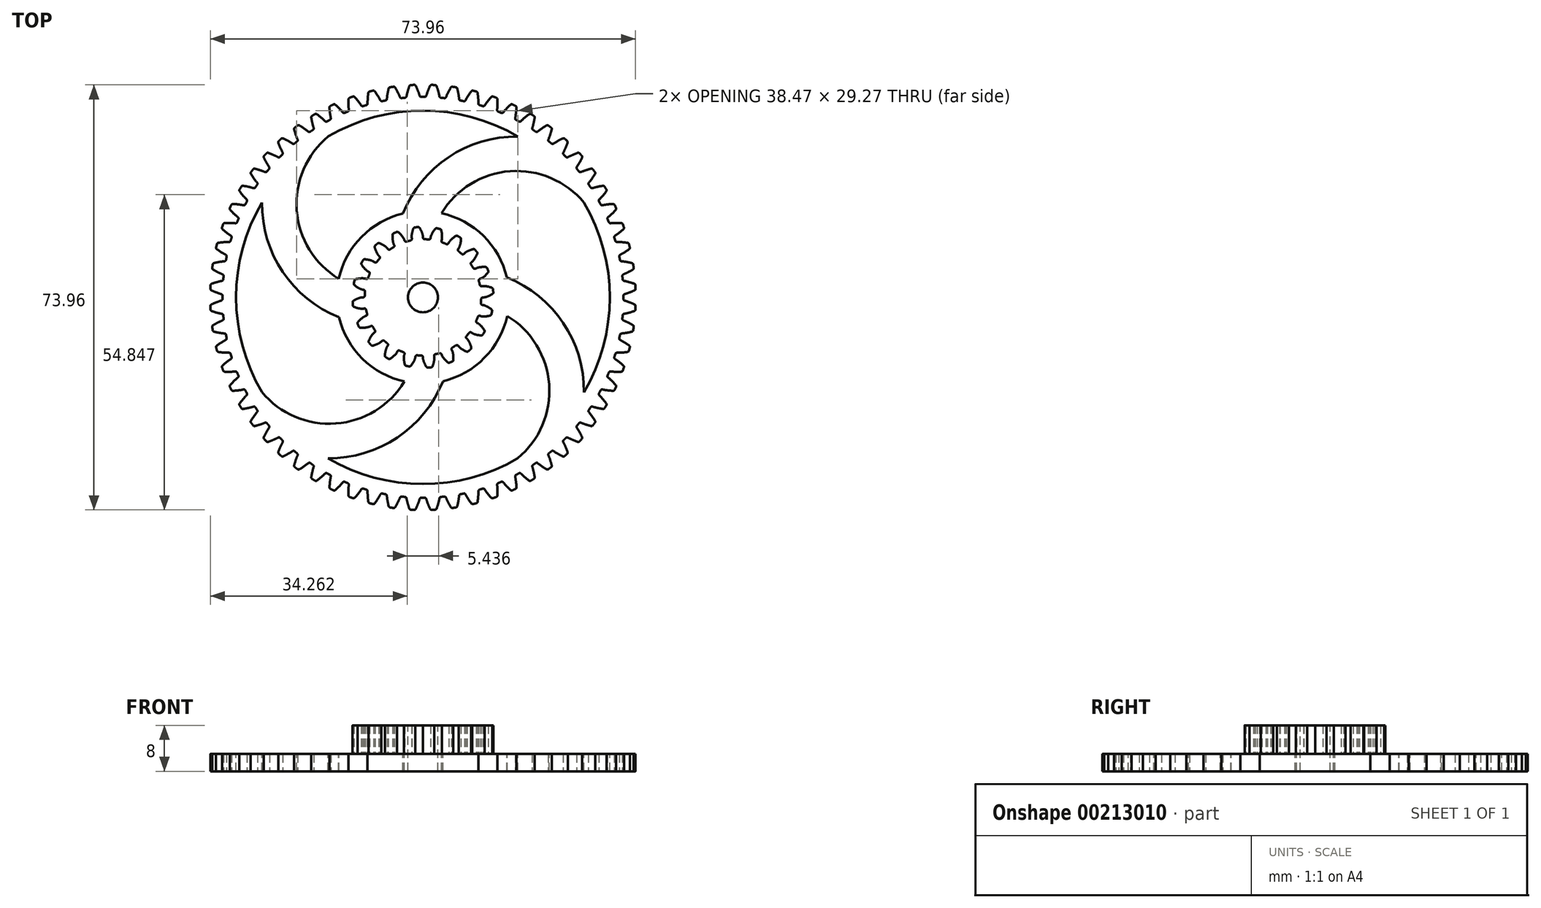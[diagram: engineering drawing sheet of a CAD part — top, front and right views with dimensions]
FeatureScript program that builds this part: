
annotation { "Feature Type Name" : "Feature", "Feature Type Description" : "" }
export const myFeature = defineFeature(function(context is Context, id is Id, definition is map)
    precondition{}
    {
        {
            var Q0;
            Q0=qCreatedBy(makeId("Top.planeOp"),FACE);
            var sketch = newSketch(context, id + "F0", { "sketchPlane" : qUnion([Q0])});
            skCircle(sketch, "E0", {"center": v(0, 0) * mm, "radius": 33.83 * mm, "construction": true});
            skLineSegment(sketch, "E1", {"start": v(0, 0) * mm, "end": v(33.83, 0) * mm, "construction": true});
            skLineSegment(sketch, "E2", {"start": v(33.83, 0) * mm, "end": v(33.83, 0) * mm});
            skLineSegment(sketch, "E3", {"start": v(0, 0) * mm, "end": v(33.79, 1.71) * mm, "construction": true});
            skLineSegment(sketch, "E4", {"start": v(33.79, 1.71) * mm, "end": v(33.87, 0) * mm, "construction": true});
            skLineSegment(sketch, "E5", {"start": v(0, 0) * mm, "end": v(33.66, 3.42) * mm, "construction": true});
            skLineSegment(sketch, "E6", {"start": v(33.66, 3.42) * mm, "end": v(34, 0.01) * mm, "construction": true});
            skLineSegment(sketch, "E7", {"start": v(0, 0) * mm, "end": v(33.44, 5.12) * mm, "construction": true});
            skLineSegment(sketch, "E8", {"start": v(33.44, 5.12) * mm, "end": v(34.22, 0.04) * mm, "construction": true});
            skLineSegment(sketch, "E9", {"start": v(0, 0) * mm, "end": v(33.14, 6.8) * mm, "construction": true});
            skLineSegment(sketch, "E10", {"start": v(33.14, 6.8) * mm, "end": v(34.52, 0.1) * mm, "construction": true});
            skLineSegment(sketch, "E11", {"start": v(0, 0) * mm, "end": v(32.75, 8.47) * mm, "construction": true});
            skLineSegment(sketch, "E12", {"start": v(32.75, 8.47) * mm, "end": v(34.9, 0.18) * mm, "construction": true});
            skLineSegment(sketch, "E13", {"start": v(0, 0) * mm, "end": v(32.28, 10.12) * mm, "construction": true});
            skLineSegment(sketch, "E14", {"start": v(32.28, 10.12) * mm, "end": v(35.35, 0.31) * mm, "construction": true});
            skLineSegment(sketch, "E15", {"start": v(0, 0) * mm, "end": v(31.73, 11.74) * mm, "construction": true});
            skLineSegment(sketch, "E16", {"start": v(31.73, 11.74) * mm, "end": v(35.89, 0.5) * mm, "construction": true});
            skLineSegment(sketch, "E17", {"start": v(0, 0) * mm, "end": v(31.1, 13.33) * mm, "construction": true});
            skLineSegment(sketch, "E18", {"start": v(31.1, 13.33) * mm, "end": v(36.49, 0.74) * mm, "construction": true});
            skLineSegment(sketch, "E19", {"start": v(0, 0) * mm, "end": v(30.38, 14.88) * mm, "construction": true});
            skLineSegment(sketch, "E20", {"start": v(30.38, 14.88) * mm, "end": v(37.16, 1.04) * mm, "construction": true});
            skLineSegment(sketch, "E21", {"start": v(0, 0) * mm, "end": v(29.59, 16.4) * mm, "construction": true});
            skLineSegment(sketch, "E22", {"start": v(29.59, 16.4) * mm, "end": v(37.89, 1.43) * mm, "construction": true});
            skPoint(sketch, "E23", {"position": v(33.83, 0) * mm});
            skCircle(sketch, "E24", {"center": v(0, 0) * mm, "radius": 34.87 * mm});
            skFitSpline(sketch, "E25", {"points": [v(33.83, 0) * mm, v(33.87, 0) * mm, v(34, 0.01) * mm, v(34.22, 0.04) * mm, v(34.52, 0.1) * mm, v(34.9, 0.18) * mm, v(35.35, 0.31) * mm, v(35.89, 0.5) * mm, v(36.49, 0.74) * mm, v(37.16, 1.04) * mm, v(37.89, 1.43) * mm], "startDerivative": vector(1.13, 0.02) * mm, "endDerivative": vector(5.03, 2.7) * mm, "construction": true});
            skFitSpline(sketch, "E26", {"points": [v(33.83, 0) * mm, v(33.87, 0) * mm, v(34, 0.01) * mm, v(34.22, 0.04) * mm, v(34.52, 0.1) * mm, v(34.9, 0.18) * mm, v(35.35, 0.31) * mm, v(35.89, 0.5) * mm, v(36.49, 0.74) * mm, v(37.16, 1.04) * mm, v(37.89, 1.43) * mm], "startDerivative": vector(1.13, 0.02) * mm, "endDerivative": vector(5.03, 2.7) * mm});
            skLineSegment(sketch, "E27", {"start": v(0, 0) * mm, "end": v(41, 1.62) * mm, "construction": true});
            skFitSpline(sketch, "E28.MirrorCS", {"points": [v(33.72, 2.67) * mm, v(33.77, 2.67) * mm, v(33.9, 2.67) * mm, v(34.11, 2.66) * mm, v(34.42, 2.63) * mm, v(34.8, 2.57) * mm, v(35.27, 2.47) * mm, v(35.81, 2.33) * mm, v(36.43, 2.14) * mm, v(37.13, 1.89) * mm, v(37.88, 1.57) * mm], "startDerivative": vector(1.13, 0.07) * mm, "endDerivative": vector(5.23, -2.3) * mm});
            skArc(sketch, "E29", {"start": v(36.96, 1.95) * mm, "mid": v(-36.98, -1.46) * mm, "end": v(37, 0.97) * mm, "construction": true});
            skArc(sketch, "E30", {"start": v(37, 0.97) * mm, "mid": v(36.98, 1.46) * mm, "end": v(36.96, 1.95) * mm});
            skSolve(sketch);
        }
        {
            var Q0;
            {var subQ0=sQuery(id+"F0.wireOp",EDGE,"E24");var subQ1=makeQuery(id+"F0.imprint","INTERSECT",VERTEX,{"derivedFrom":[subQ0,sQuery(id+"F0.wireOp",EDGE,"E26")]});Q0=makeQuery(id+"F0.imprint","IMPRINT",FACE,{"disambiguationData":[TD([[makeQuery(id+"F0.imprint","IMPRINT",EDGE,{"disambiguationData":[TD([[subQ1,-1.0]])],"derivedFrom":subQ0}),1.0]])]});}
            var Q1;
            {var subQ0=sQuery(id+"F0.wireOp",EDGE,"E26");Q1=makeQuery(id+"F0.imprint","IMPRINT",FACE,{"disambiguationData":[TD([[makeQuery(id+"F0.imprint","IMPRINT",EDGE,{"derivedFrom":subQ0}),1.0]])]});}
            extrude(context, id + "F1", {"entities" : qUnion([Q0, Q1]), "depth" : 3 * mm});
        }
        {
            var Q0;
            Q0=qCreatedBy(makeId("Front.planeOp"),FACE);
            var sketch = newSketch(context, id + "F2", { "sketchPlane" : qUnion([Q0])});
            skLineSegment(sketch, "E31", {"start": v(0, 0) * mm, "end": v(0, 31.12) * mm});
            skSolve(sketch);
        }
        {
            var Q0;
            Q0=makeQuery(id+"F1.opExtrude","SWEPT_EDGE",EDGE,{"disambiguationData":[OSD([sQuery(id+"F0.wireOp",EDGE,"E24"),sQuery(id+"F0.wireOp",EDGE,"E26")])]});
            var Q1;
            Q1=makeQuery(id+"F1.opExtrude","SWEPT_EDGE",EDGE,{"disambiguationData":[OSD([sQuery(id+"F0.wireOp",EDGE,"E26"),sQuery(id+"F0.wireOp",EDGE,"E30")])]});
            var Q2;
            Q2=makeQuery(id+"F1.opExtrude","SWEPT_EDGE",EDGE,{"disambiguationData":[OSD([sQuery(id+"F0.wireOp",EDGE,"E28.MirrorCS"),sQuery(id+"F0.wireOp",EDGE,"E30")])]});
            var Q3;
            Q3=makeQuery(id+"F1.opExtrude","SWEPT_EDGE",EDGE,{"disambiguationData":[OSD([sQuery(id+"F0.wireOp",EDGE,"E24"),sQuery(id+"F0.wireOp",EDGE,"E28.MirrorCS")])]});
            fillet(context, id + "F3", {"entities" : qUnion([Q0, Q1, Q2, Q3]), "radius" : 0.3 * mm, "tangentPropagation" : true, "allowEdgeOverflow" : false});
        }
        {
            var Q0;
            Q0=makeQuery(id+"F1.opExtrude","SWEPT_BODY",BODY,{"disambiguationData":[OSD([sQuery(id+"F0.wireOp",EDGE,"E24"),sQuery(id+"F0.wireOp",EDGE,"E26"),sQuery(id+"F0.wireOp",EDGE,"E28.MirrorCS"),sQuery(id+"F0.wireOp",EDGE,"E30")])]});
            var Q1;
            Q1=sQuery(id+"F2.wireOp",EDGE,"E31");
            circularPattern(context, id + "F4", {"operationType" : NewBodyOperationType.ADD, "entities" : qUnion([Q0]), "axis" : qUnion([Q1]), "angle" : 360 * degree, "instanceCount" : 64, "equalSpace" : true});
        }
        {
            var Q0;
            {var subQ0=makeQuery(id+"F1.opExtrude","CAP_FACE",FACE,{"disambiguationData":[OSD([sQuery(id+"F0.wireOp",EDGE,"E24"),sQuery(id+"F0.wireOp",EDGE,"E26"),sQuery(id+"F0.wireOp",EDGE,"E28.MirrorCS"),sQuery(id+"F0.wireOp",EDGE,"E30")])],"isStart":false});Q0=makeQuery(id+"F4.boolean.opBoolean","MERGE",FACE,{"derivedFrom":[subQ0,makeQuery(id+"F4.opPattern","COPY",FACE,{"derivedFrom":subQ0,"instanceName":"1"}),makeQuery(id+"F4.opPattern","COPY",FACE,{"derivedFrom":subQ0,"instanceName":"2"}),makeQuery(id+"F4.opPattern","COPY",FACE,{"derivedFrom":subQ0,"instanceName":"3"}),makeQuery(id+"F4.opPattern","COPY",FACE,{"derivedFrom":subQ0,"instanceName":"4"}),makeQuery(id+"F4.opPattern","COPY",FACE,{"derivedFrom":subQ0,"instanceName":"5"}),makeQuery(id+"F4.opPattern","COPY",FACE,{"derivedFrom":subQ0,"instanceName":"6"}),makeQuery(id+"F4.opPattern","COPY",FACE,{"derivedFrom":subQ0,"instanceName":"7"}),makeQuery(id+"F4.opPattern","COPY",FACE,{"derivedFrom":subQ0,"instanceName":"8"}),makeQuery(id+"F4.opPattern","COPY",FACE,{"derivedFrom":subQ0,"instanceName":"9"}),makeQuery(id+"F4.opPattern","COPY",FACE,{"derivedFrom":subQ0,"instanceName":"10"}),makeQuery(id+"F4.opPattern","COPY",FACE,{"derivedFrom":subQ0,"instanceName":"11"}),makeQuery(id+"F4.opPattern","COPY",FACE,{"derivedFrom":subQ0,"instanceName":"12"}),makeQuery(id+"F4.opPattern","COPY",FACE,{"derivedFrom":subQ0,"instanceName":"13"}),makeQuery(id+"F4.opPattern","COPY",FACE,{"derivedFrom":subQ0,"instanceName":"14"}),makeQuery(id+"F4.opPattern","COPY",FACE,{"derivedFrom":subQ0,"instanceName":"15"}),makeQuery(id+"F4.opPattern","COPY",FACE,{"derivedFrom":subQ0,"instanceName":"16"}),makeQuery(id+"F4.opPattern","COPY",FACE,{"derivedFrom":subQ0,"instanceName":"17"}),makeQuery(id+"F4.opPattern","COPY",FACE,{"derivedFrom":subQ0,"instanceName":"18"}),makeQuery(id+"F4.opPattern","COPY",FACE,{"derivedFrom":subQ0,"instanceName":"19"}),makeQuery(id+"F4.opPattern","COPY",FACE,{"derivedFrom":subQ0,"instanceName":"20"}),makeQuery(id+"F4.opPattern","COPY",FACE,{"derivedFrom":subQ0,"instanceName":"21"}),makeQuery(id+"F4.opPattern","COPY",FACE,{"derivedFrom":subQ0,"instanceName":"22"}),makeQuery(id+"F4.opPattern","COPY",FACE,{"derivedFrom":subQ0,"instanceName":"23"}),makeQuery(id+"F4.opPattern","COPY",FACE,{"derivedFrom":subQ0,"instanceName":"24"}),makeQuery(id+"F4.opPattern","COPY",FACE,{"derivedFrom":subQ0,"instanceName":"25"}),makeQuery(id+"F4.opPattern","COPY",FACE,{"derivedFrom":subQ0,"instanceName":"26"}),makeQuery(id+"F4.opPattern","COPY",FACE,{"derivedFrom":subQ0,"instanceName":"27"}),makeQuery(id+"F4.opPattern","COPY",FACE,{"derivedFrom":subQ0,"instanceName":"28"}),makeQuery(id+"F4.opPattern","COPY",FACE,{"derivedFrom":subQ0,"instanceName":"29"}),makeQuery(id+"F4.opPattern","COPY",FACE,{"derivedFrom":subQ0,"instanceName":"30"}),makeQuery(id+"F4.opPattern","COPY",FACE,{"derivedFrom":subQ0,"instanceName":"31"}),makeQuery(id+"F4.opPattern","COPY",FACE,{"derivedFrom":subQ0,"instanceName":"32"}),makeQuery(id+"F4.opPattern","COPY",FACE,{"derivedFrom":subQ0,"instanceName":"33"}),makeQuery(id+"F4.opPattern","COPY",FACE,{"derivedFrom":subQ0,"instanceName":"34"}),makeQuery(id+"F4.opPattern","COPY",FACE,{"derivedFrom":subQ0,"instanceName":"35"}),makeQuery(id+"F4.opPattern","COPY",FACE,{"derivedFrom":subQ0,"instanceName":"36"}),makeQuery(id+"F4.opPattern","COPY",FACE,{"derivedFrom":subQ0,"instanceName":"37"}),makeQuery(id+"F4.opPattern","COPY",FACE,{"derivedFrom":subQ0,"instanceName":"38"}),makeQuery(id+"F4.opPattern","COPY",FACE,{"derivedFrom":subQ0,"instanceName":"39"}),makeQuery(id+"F4.opPattern","COPY",FACE,{"derivedFrom":subQ0,"instanceName":"40"}),makeQuery(id+"F4.opPattern","COPY",FACE,{"derivedFrom":subQ0,"instanceName":"41"}),makeQuery(id+"F4.opPattern","COPY",FACE,{"derivedFrom":subQ0,"instanceName":"42"}),makeQuery(id+"F4.opPattern","COPY",FACE,{"derivedFrom":subQ0,"instanceName":"43"}),makeQuery(id+"F4.opPattern","COPY",FACE,{"derivedFrom":subQ0,"instanceName":"44"}),makeQuery(id+"F4.opPattern","COPY",FACE,{"derivedFrom":subQ0,"instanceName":"45"}),makeQuery(id+"F4.opPattern","COPY",FACE,{"derivedFrom":subQ0,"instanceName":"46"}),makeQuery(id+"F4.opPattern","COPY",FACE,{"derivedFrom":subQ0,"instanceName":"47"}),makeQuery(id+"F4.opPattern","COPY",FACE,{"derivedFrom":subQ0,"instanceName":"48"}),makeQuery(id+"F4.opPattern","COPY",FACE,{"derivedFrom":subQ0,"instanceName":"49"}),makeQuery(id+"F4.opPattern","COPY",FACE,{"derivedFrom":subQ0,"instanceName":"50"}),makeQuery(id+"F4.opPattern","COPY",FACE,{"derivedFrom":subQ0,"instanceName":"51"}),makeQuery(id+"F4.opPattern","COPY",FACE,{"derivedFrom":subQ0,"instanceName":"52"}),makeQuery(id+"F4.opPattern","COPY",FACE,{"derivedFrom":subQ0,"instanceName":"53"}),makeQuery(id+"F4.opPattern","COPY",FACE,{"derivedFrom":subQ0,"instanceName":"54"}),makeQuery(id+"F4.opPattern","COPY",FACE,{"derivedFrom":subQ0,"instanceName":"55"}),makeQuery(id+"F4.opPattern","COPY",FACE,{"derivedFrom":subQ0,"instanceName":"56"}),makeQuery(id+"F4.opPattern","COPY",FACE,{"derivedFrom":subQ0,"instanceName":"57"}),makeQuery(id+"F4.opPattern","COPY",FACE,{"derivedFrom":subQ0,"instanceName":"58"}),makeQuery(id+"F4.opPattern","COPY",FACE,{"derivedFrom":subQ0,"instanceName":"59"}),makeQuery(id+"F4.opPattern","COPY",FACE,{"derivedFrom":subQ0,"instanceName":"60"}),makeQuery(id+"F4.opPattern","COPY",FACE,{"derivedFrom":subQ0,"instanceName":"61"}),makeQuery(id+"F4.opPattern","COPY",FACE,{"derivedFrom":subQ0,"instanceName":"62"}),makeQuery(id+"F4.opPattern","COPY",FACE,{"derivedFrom":subQ0,"instanceName":"63"})]});}
            var sketch = newSketch(context, id + "F5", { "sketchPlane" : qUnion([Q0])});
            skLineSegment(sketch, "E32", {"start": v(0, 0) * mm, "end": v(34.87, -0.34) * mm, "construction": true});
            skCircle(sketch, "E33", {"center": v(0, 0) * mm, "radius": 10.57 * mm, "construction": true});
            skLineSegment(sketch, "E34", {"start": v(6.13, 8.61) * mm, "end": v(6.13, 8.61) * mm});
            skLineSegment(sketch, "E35", {"start": v(0, 0) * mm, "end": v(10.55, 0.65) * mm, "construction": true});
            skLineSegment(sketch, "E36", {"start": v(10.55, 0.65) * mm, "end": v(10.6, 0) * mm, "construction": true});
            skLineSegment(sketch, "E37", {"start": v(0, 0) * mm, "end": v(10.5, 1.29) * mm, "construction": true});
            skLineSegment(sketch, "E38", {"start": v(10.5, 1.29) * mm, "end": v(10.65, 0) * mm, "construction": true});
            skLineSegment(sketch, "E39", {"start": v(0, 0) * mm, "end": v(10.4, 1.93) * mm, "construction": true});
            skLineSegment(sketch, "E40", {"start": v(10.4, 1.93) * mm, "end": v(10.75, 0.02) * mm, "construction": true});
            skLineSegment(sketch, "E41", {"start": v(0, 0) * mm, "end": v(10.26, 2.56) * mm, "construction": true});
            skLineSegment(sketch, "E42", {"start": v(10.26, 2.56) * mm, "end": v(10.88, 0.05) * mm, "construction": true});
            skLineSegment(sketch, "E43", {"start": v(0, 0) * mm, "end": v(10.08, 3.18) * mm, "construction": true});
            skLineSegment(sketch, "E44", {"start": v(10.08, 3.18) * mm, "end": v(11.05, 0.1) * mm, "construction": true});
            skLineSegment(sketch, "E45", {"start": v(0, 0) * mm, "end": v(9.87, 3.79) * mm, "construction": true});
            skLineSegment(sketch, "E46", {"start": v(9.87, 3.79) * mm, "end": v(11.26, 0.17) * mm, "construction": true});
            skLineSegment(sketch, "E47", {"start": v(0, 0) * mm, "end": v(9.62, 4.38) * mm, "construction": true});
            skLineSegment(sketch, "E48", {"start": v(9.62, 4.38) * mm, "end": v(11.5, 0.27) * mm, "construction": true});
            skLineSegment(sketch, "E49", {"start": v(0, 0) * mm, "end": v(9.33, 4.96) * mm, "construction": true});
            skLineSegment(sketch, "E50", {"start": v(9.33, 4.96) * mm, "end": v(11.76, 0.4) * mm, "construction": true});
            skLineSegment(sketch, "E51", {"start": v(0, 0) * mm, "end": v(9.01, 5.52) * mm, "construction": true});
            skLineSegment(sketch, "E52", {"start": v(9.01, 5.52) * mm, "end": v(12.05, 0.57) * mm, "construction": true});
            skLineSegment(sketch, "E53", {"start": v(0, 0) * mm, "end": v(8.66, 6.06) * mm, "construction": true});
            skLineSegment(sketch, "E54", {"start": v(8.66, 6.06) * mm, "end": v(12.36, 0.77) * mm, "construction": true});
            skPoint(sketch, "E55", {"position": v(10.57, 0) * mm});
            skCircle(sketch, "E56", {"center": v(0, 0) * mm, "radius": 10.12 * mm});
            skLineSegment(sketch, "E57", {"start": v(10.12, 0) * mm, "end": v(10.57, 0) * mm});
            skFitSpline(sketch, "E58", {"points": [v(10.57, 0) * mm, v(10.6, 0) * mm, v(10.65, 0) * mm, v(10.75, 0.02) * mm, v(10.88, 0.05) * mm, v(11.05, 0.1) * mm, v(11.26, 0.17) * mm, v(11.5, 0.27) * mm, v(11.76, 0.4) * mm, v(12.05, 0.57) * mm, v(12.36, 0.77) * mm], "startDerivative": vector(0.52, 0.01) * mm, "endDerivative": vector(2.16, 1.45) * mm});
            skFitSpline(sketch, "E59", {"points": [v(10.57, 0) * mm, v(10.6, 0) * mm, v(10.65, 0) * mm, v(10.75, 0.02) * mm, v(10.88, 0.05) * mm, v(11.05, 0.1) * mm, v(11.26, 0.17) * mm, v(11.5, 0.27) * mm, v(11.76, 0.4) * mm, v(12.05, 0.57) * mm, v(12.36, 0.77) * mm], "startDerivative": vector(0.52, 0.01) * mm, "endDerivative": vector(2.16, 1.45) * mm, "construction": true});
            skLineSegment(sketch, "E60", {"start": v(0, 0) * mm, "end": v(14, 1.31) * mm, "construction": true});
            skLineSegment(sketch, "E61.MirrorCS", {"start": v(9.95, 1.88) * mm, "end": v(10.39, 1.96) * mm});
            skFitSpline(sketch, "E62.MirrorCS", {"points": [v(10.39, 1.96) * mm, v(10.4, 1.97) * mm, v(10.47, 1.97) * mm, v(10.56, 1.98) * mm, v(10.7, 1.97) * mm, v(10.88, 1.96) * mm, v(11.1, 1.92) * mm, v(11.34, 1.87) * mm, v(11.63, 1.8) * mm, v(11.95, 1.68) * mm, v(12.3, 1.54) * mm], "startDerivative": vector(0.5, 0.08) * mm, "endDerivative": vector(2.39, -1.03) * mm});
            skArc(sketch, "E63", {"start": v(12.16, 1.6) * mm, "mid": v(-12.2, -1.14) * mm, "end": v(12.24, 0.7) * mm, "construction": true});
            skArc(sketch, "E64", {"start": v(12.24, 0.7) * mm, "mid": v(12.2, 1.14) * mm, "end": v(12.16, 1.6) * mm});
            skSolve(sketch);
        }
        {
            var Q0;
            {var subQ0=sQuery(id+"F5.wireOp",EDGE,"E56");var subQ1=makeQuery(id+"F5.imprint","INTERSECT",VERTEX,{"derivedFrom":[subQ0,sQuery(id+"F5.wireOp",EDGE,"E57")]});Q0=makeQuery(id+"F5.imprint","IMPRINT",FACE,{"disambiguationData":[TD([[makeQuery(id+"F5.imprint","IMPRINT",EDGE,{"disambiguationData":[TD([[subQ1,-1.0]])],"derivedFrom":subQ0}),1.0]])]});}
            var Q1;
            {var subQ1=sQuery(id+"F5.wireOp",EDGE,"E57");Q1=makeQuery(id+"F5.imprint","IMPRINT",FACE,{"disambiguationData":[TD([[makeQuery(id+"F5.imprint","IMPRINT",EDGE,{"derivedFrom":subQ1}),1.0]])]});}
            extrude(context, id + "F6", {"entities" : qUnion([Q0, Q1]), "depth" : 5 * mm});
        }
        {
            var Q0;
            Q0=makeQuery(id+"F1.opExtrude","SWEPT_BODY",BODY,{"disambiguationData":[OSD([sQuery(id+"F0.wireOp",EDGE,"E24"),sQuery(id+"F0.wireOp",EDGE,"E26"),sQuery(id+"F0.wireOp",EDGE,"E28.MirrorCS"),sQuery(id+"F0.wireOp",EDGE,"E30")])]});
            var Q1;
            Q1=sQuery(id+"F2.wireOp",EDGE,"E31");
            transform(context, id + "F7", {"entities" : qUnion([Q0]), "transformType" : TransformType.ROTATION, "transformAxis" : qUnion([Q1]), "angle" : 0.55 * degree, "makeCopy" : false});
        }
        {
            var Q0;
            Q0=makeQuery(id+"F6.opExtrude","SWEPT_EDGE",EDGE,{"disambiguationData":[OSD([sQuery(id+"F5.wireOp",EDGE,"E58"),sQuery(id+"F5.wireOp",EDGE,"E64")])]});
            var Q1;
            Q1=makeQuery(id+"F6.opExtrude","SWEPT_EDGE",EDGE,{"disambiguationData":[OSD([sQuery(id+"F5.wireOp",EDGE,"E56"),sQuery(id+"F5.wireOp",EDGE,"E57")])]});
            var Q2;
            Q2=makeQuery(id+"F6.opExtrude","SWEPT_EDGE",EDGE,{"disambiguationData":[OSD([sQuery(id+"F5.wireOp",EDGE,"E62.MirrorCS"),sQuery(id+"F5.wireOp",EDGE,"E64")])]});
            var Q3;
            Q3=makeQuery(id+"F6.opExtrude","SWEPT_EDGE",EDGE,{"disambiguationData":[OSD([sQuery(id+"F5.wireOp",EDGE,"E56"),sQuery(id+"F5.wireOp",EDGE,"E61.MirrorCS")])]});
            fillet(context, id + "F8", {"entities" : qUnion([Q0, Q1, Q2, Q3]), "radius" : 0.3 * mm, "tangentPropagation" : true, "allowEdgeOverflow" : false});
        }
        {
            var Q0;
            Q0=makeQuery(id+"F6.opExtrude","SWEPT_BODY",BODY,{"disambiguationData":[OSD([sQuery(id+"F5.wireOp",EDGE,"E56"),sQuery(id+"F5.wireOp",EDGE,"E57"),sQuery(id+"F5.wireOp",EDGE,"E58"),sQuery(id+"F5.wireOp",EDGE,"E61.MirrorCS"),sQuery(id+"F5.wireOp",EDGE,"E62.MirrorCS"),sQuery(id+"F5.wireOp",EDGE,"E64")])]});
            var Q1;
            Q1=sQuery(id+"F2.wireOp",EDGE,"E31");
            circularPattern(context, id + "F9", {"operationType" : NewBodyOperationType.ADD, "entities" : qUnion([Q0]), "axis" : qUnion([Q1]), "angle" : 360 * degree, "instanceCount" : 20, "equalSpace" : true});
        }
        {
            var Q0;
            {var subQ0=makeQuery(id+"F6.opExtrude","CAP_FACE",FACE,{"disambiguationData":[OSD([sQuery(id+"F5.wireOp",EDGE,"E56"),sQuery(id+"F5.wireOp",EDGE,"E57"),sQuery(id+"F5.wireOp",EDGE,"E58"),sQuery(id+"F5.wireOp",EDGE,"E61.MirrorCS"),sQuery(id+"F5.wireOp",EDGE,"E62.MirrorCS"),sQuery(id+"F5.wireOp",EDGE,"E64")])],"isStart":false});Q0=makeQuery(id+"F9.boolean.opBoolean","MERGE",FACE,{"derivedFrom":[subQ0,makeQuery(id+"F9.opPattern","COPY",FACE,{"derivedFrom":subQ0,"instanceName":"1"}),makeQuery(id+"F9.opPattern","COPY",FACE,{"derivedFrom":subQ0,"instanceName":"2"}),makeQuery(id+"F9.opPattern","COPY",FACE,{"derivedFrom":subQ0,"instanceName":"3"}),makeQuery(id+"F9.opPattern","COPY",FACE,{"derivedFrom":subQ0,"instanceName":"4"}),makeQuery(id+"F9.opPattern","COPY",FACE,{"derivedFrom":subQ0,"instanceName":"5"}),makeQuery(id+"F9.opPattern","COPY",FACE,{"derivedFrom":subQ0,"instanceName":"6"}),makeQuery(id+"F9.opPattern","COPY",FACE,{"derivedFrom":subQ0,"instanceName":"7"}),makeQuery(id+"F9.opPattern","COPY",FACE,{"derivedFrom":subQ0,"instanceName":"8"}),makeQuery(id+"F9.opPattern","COPY",FACE,{"derivedFrom":subQ0,"instanceName":"9"}),makeQuery(id+"F9.opPattern","COPY",FACE,{"derivedFrom":subQ0,"instanceName":"10"}),makeQuery(id+"F9.opPattern","COPY",FACE,{"derivedFrom":subQ0,"instanceName":"11"}),makeQuery(id+"F9.opPattern","COPY",FACE,{"derivedFrom":subQ0,"instanceName":"12"}),makeQuery(id+"F9.opPattern","COPY",FACE,{"derivedFrom":subQ0,"instanceName":"13"}),makeQuery(id+"F9.opPattern","COPY",FACE,{"derivedFrom":subQ0,"instanceName":"14"}),makeQuery(id+"F9.opPattern","COPY",FACE,{"derivedFrom":subQ0,"instanceName":"15"}),makeQuery(id+"F9.opPattern","COPY",FACE,{"derivedFrom":subQ0,"instanceName":"16"}),makeQuery(id+"F9.opPattern","COPY",FACE,{"derivedFrom":subQ0,"instanceName":"17"}),makeQuery(id+"F9.opPattern","COPY",FACE,{"derivedFrom":subQ0,"instanceName":"18"}),makeQuery(id+"F9.opPattern","COPY",FACE,{"derivedFrom":subQ0,"instanceName":"19"})]});}
            var sketch = newSketch(context, id + "F10", { "sketchPlane" : qUnion([Q0])});
            skCircle(sketch, "E65", {"center": v(0, 0) * mm, "radius": 2.6 * mm});
            skSolve(sketch);
        }
        {
            var Q0;
            Q0=makeQuery(id+"F10.imprint","IMPRINT",FACE,{"disambiguationData":[TD([[makeQuery(id+"F10.imprint","IMPRINT",EDGE,{"derivedFrom":sQuery(id+"F10.wireOp",EDGE,"E65")}),1.0]])]});
            extrude(context, id + "F11", {"entities" : qUnion([Q0]), "operationType" : NewBodyOperationType.REMOVE, "endBound" : BoundingType.UP_TO_NEXT, "oppositeDirection" : true, "depth" : 25 * mm});
        }
        {
            var Q0;
            {var subQ0=makeQuery(id+"F1.opExtrude","CAP_FACE",FACE,{"disambiguationData":[OSD([sQuery(id+"F0.wireOp",EDGE,"E24"),sQuery(id+"F0.wireOp",EDGE,"E26"),sQuery(id+"F0.wireOp",EDGE,"E28.MirrorCS"),sQuery(id+"F0.wireOp",EDGE,"E30")])],"isStart":false});Q0=makeQuery(id+"F4.boolean.opBoolean","MERGE",FACE,{"derivedFrom":[subQ0,makeQuery(id+"F4.opPattern","COPY",FACE,{"derivedFrom":subQ0,"instanceName":"1"}),makeQuery(id+"F4.opPattern","COPY",FACE,{"derivedFrom":subQ0,"instanceName":"2"}),makeQuery(id+"F4.opPattern","COPY",FACE,{"derivedFrom":subQ0,"instanceName":"3"}),makeQuery(id+"F4.opPattern","COPY",FACE,{"derivedFrom":subQ0,"instanceName":"4"}),makeQuery(id+"F4.opPattern","COPY",FACE,{"derivedFrom":subQ0,"instanceName":"5"}),makeQuery(id+"F4.opPattern","COPY",FACE,{"derivedFrom":subQ0,"instanceName":"6"}),makeQuery(id+"F4.opPattern","COPY",FACE,{"derivedFrom":subQ0,"instanceName":"7"}),makeQuery(id+"F4.opPattern","COPY",FACE,{"derivedFrom":subQ0,"instanceName":"8"}),makeQuery(id+"F4.opPattern","COPY",FACE,{"derivedFrom":subQ0,"instanceName":"9"}),makeQuery(id+"F4.opPattern","COPY",FACE,{"derivedFrom":subQ0,"instanceName":"10"}),makeQuery(id+"F4.opPattern","COPY",FACE,{"derivedFrom":subQ0,"instanceName":"11"}),makeQuery(id+"F4.opPattern","COPY",FACE,{"derivedFrom":subQ0,"instanceName":"12"}),makeQuery(id+"F4.opPattern","COPY",FACE,{"derivedFrom":subQ0,"instanceName":"13"}),makeQuery(id+"F4.opPattern","COPY",FACE,{"derivedFrom":subQ0,"instanceName":"14"}),makeQuery(id+"F4.opPattern","COPY",FACE,{"derivedFrom":subQ0,"instanceName":"15"}),makeQuery(id+"F4.opPattern","COPY",FACE,{"derivedFrom":subQ0,"instanceName":"16"}),makeQuery(id+"F4.opPattern","COPY",FACE,{"derivedFrom":subQ0,"instanceName":"17"}),makeQuery(id+"F4.opPattern","COPY",FACE,{"derivedFrom":subQ0,"instanceName":"18"}),makeQuery(id+"F4.opPattern","COPY",FACE,{"derivedFrom":subQ0,"instanceName":"19"}),makeQuery(id+"F4.opPattern","COPY",FACE,{"derivedFrom":subQ0,"instanceName":"20"}),makeQuery(id+"F4.opPattern","COPY",FACE,{"derivedFrom":subQ0,"instanceName":"21"}),makeQuery(id+"F4.opPattern","COPY",FACE,{"derivedFrom":subQ0,"instanceName":"22"}),makeQuery(id+"F4.opPattern","COPY",FACE,{"derivedFrom":subQ0,"instanceName":"23"}),makeQuery(id+"F4.opPattern","COPY",FACE,{"derivedFrom":subQ0,"instanceName":"24"}),makeQuery(id+"F4.opPattern","COPY",FACE,{"derivedFrom":subQ0,"instanceName":"25"}),makeQuery(id+"F4.opPattern","COPY",FACE,{"derivedFrom":subQ0,"instanceName":"26"}),makeQuery(id+"F4.opPattern","COPY",FACE,{"derivedFrom":subQ0,"instanceName":"27"}),makeQuery(id+"F4.opPattern","COPY",FACE,{"derivedFrom":subQ0,"instanceName":"28"}),makeQuery(id+"F4.opPattern","COPY",FACE,{"derivedFrom":subQ0,"instanceName":"29"}),makeQuery(id+"F4.opPattern","COPY",FACE,{"derivedFrom":subQ0,"instanceName":"30"}),makeQuery(id+"F4.opPattern","COPY",FACE,{"derivedFrom":subQ0,"instanceName":"31"}),makeQuery(id+"F4.opPattern","COPY",FACE,{"derivedFrom":subQ0,"instanceName":"32"}),makeQuery(id+"F4.opPattern","COPY",FACE,{"derivedFrom":subQ0,"instanceName":"33"}),makeQuery(id+"F4.opPattern","COPY",FACE,{"derivedFrom":subQ0,"instanceName":"34"}),makeQuery(id+"F4.opPattern","COPY",FACE,{"derivedFrom":subQ0,"instanceName":"35"}),makeQuery(id+"F4.opPattern","COPY",FACE,{"derivedFrom":subQ0,"instanceName":"36"}),makeQuery(id+"F4.opPattern","COPY",FACE,{"derivedFrom":subQ0,"instanceName":"37"}),makeQuery(id+"F4.opPattern","COPY",FACE,{"derivedFrom":subQ0,"instanceName":"38"}),makeQuery(id+"F4.opPattern","COPY",FACE,{"derivedFrom":subQ0,"instanceName":"39"}),makeQuery(id+"F4.opPattern","COPY",FACE,{"derivedFrom":subQ0,"instanceName":"40"}),makeQuery(id+"F4.opPattern","COPY",FACE,{"derivedFrom":subQ0,"instanceName":"41"}),makeQuery(id+"F4.opPattern","COPY",FACE,{"derivedFrom":subQ0,"instanceName":"42"}),makeQuery(id+"F4.opPattern","COPY",FACE,{"derivedFrom":subQ0,"instanceName":"43"}),makeQuery(id+"F4.opPattern","COPY",FACE,{"derivedFrom":subQ0,"instanceName":"44"}),makeQuery(id+"F4.opPattern","COPY",FACE,{"derivedFrom":subQ0,"instanceName":"45"}),makeQuery(id+"F4.opPattern","COPY",FACE,{"derivedFrom":subQ0,"instanceName":"46"}),makeQuery(id+"F4.opPattern","COPY",FACE,{"derivedFrom":subQ0,"instanceName":"47"}),makeQuery(id+"F4.opPattern","COPY",FACE,{"derivedFrom":subQ0,"instanceName":"48"}),makeQuery(id+"F4.opPattern","COPY",FACE,{"derivedFrom":subQ0,"instanceName":"49"}),makeQuery(id+"F4.opPattern","COPY",FACE,{"derivedFrom":subQ0,"instanceName":"50"}),makeQuery(id+"F4.opPattern","COPY",FACE,{"derivedFrom":subQ0,"instanceName":"51"}),makeQuery(id+"F4.opPattern","COPY",FACE,{"derivedFrom":subQ0,"instanceName":"52"}),makeQuery(id+"F4.opPattern","COPY",FACE,{"derivedFrom":subQ0,"instanceName":"53"}),makeQuery(id+"F4.opPattern","COPY",FACE,{"derivedFrom":subQ0,"instanceName":"54"}),makeQuery(id+"F4.opPattern","COPY",FACE,{"derivedFrom":subQ0,"instanceName":"55"}),makeQuery(id+"F4.opPattern","COPY",FACE,{"derivedFrom":subQ0,"instanceName":"56"}),makeQuery(id+"F4.opPattern","COPY",FACE,{"derivedFrom":subQ0,"instanceName":"57"}),makeQuery(id+"F4.opPattern","COPY",FACE,{"derivedFrom":subQ0,"instanceName":"58"}),makeQuery(id+"F4.opPattern","COPY",FACE,{"derivedFrom":subQ0,"instanceName":"59"}),makeQuery(id+"F4.opPattern","COPY",FACE,{"derivedFrom":subQ0,"instanceName":"60"}),makeQuery(id+"F4.opPattern","COPY",FACE,{"derivedFrom":subQ0,"instanceName":"61"}),makeQuery(id+"F4.opPattern","COPY",FACE,{"derivedFrom":subQ0,"instanceName":"62"}),makeQuery(id+"F4.opPattern","COPY",FACE,{"derivedFrom":subQ0,"instanceName":"63"})]});}
            var sketch = newSketch(context, id + "F12", { "sketchPlane" : qUnion([Q0])});
            skCircle(sketch, "E66", {"center": v(0, 0) * mm, "radius": 15 * mm});
            skCircle(sketch, "E67", {"center": v(0, 0) * mm, "radius": 32.5 * mm});
            skLineSegment(sketch, "E68", {"start": v(0, 0) * mm, "end": v(21.75, 24.15) * mm, "construction": true});
            skPoint(sketch, "E69.first.point", {"position": v(0, 15) * mm});
            skPoint(sketch, "E69.third.point", {"position": v(9.58, 23.72) * mm});
            skArc(sketch, "E70", {"start": v(28.02, 16.47) * mm, "mid": v(15.16, 21.95) * mm, "end": v(3.23, 14.65) * mm});
            skArc(sketch, "E71", {"start": v(21.75, 24.15) * mm, "mid": v(9.2, 23.56) * mm, "end": v(0, 15) * mm, "construction": true});
            skArc(sketch, "E72", {"start": v(0, 15) * mm, "mid": v(23.35, -10.07) * mm, "end": v(21.75, 24.15) * mm, "construction": true});
            skArc(sketch, "E73", {"start": v(16.52, 28) * mm, "mid": v(4.44, 24.4) * mm, "end": v(-3.47, 14.6) * mm});
            skArc(sketch, "E74.1.0", {"start": v(-16.47, 28.02) * mm, "mid": v(-21.95, 15.16) * mm, "end": v(-14.65, 3.23) * mm});
            skArc(sketch, "E74.1.1", {"start": v(-28, 16.52) * mm, "mid": v(-24.4, 4.44) * mm, "end": v(-14.6, -3.47) * mm});
            skArc(sketch, "E74.2.0", {"start": v(-28.02, -16.47) * mm, "mid": v(-15.16, -21.95) * mm, "end": v(-3.23, -14.65) * mm});
            skArc(sketch, "E74.2.1", {"start": v(-16.52, -28) * mm, "mid": v(-4.44, -24.4) * mm, "end": v(3.47, -14.6) * mm});
            skArc(sketch, "E74.3.0", {"start": v(16.47, -28.02) * mm, "mid": v(21.95, -15.16) * mm, "end": v(14.65, -3.23) * mm});
            skArc(sketch, "E74.3.1", {"start": v(28, -16.52) * mm, "mid": v(24.4, -4.44) * mm, "end": v(14.6, 3.47) * mm});
            skSolve(sketch);
        }
        {
            var Q0;
            {var subQ0=sQuery(id+"F12.wireOp",EDGE,"E70");Q0=makeQuery(id+"F12.imprint","IMPRINT",FACE,{"disambiguationData":[TD([[makeQuery(id+"F12.imprint","IMPRINT",EDGE,{"derivedFrom":subQ0}),1.0]])]});}
            var Q1;
            {var subQ0=sQuery(id+"F12.wireOp",EDGE,"E74.2.1");Q1=makeQuery(id+"F12.imprint","IMPRINT",FACE,{"disambiguationData":[TD([[makeQuery(id+"F12.imprint","IMPRINT",EDGE,{"derivedFrom":subQ0}),-1.0]])]});}
            var Q2;
            {var subQ0=sQuery(id+"F12.wireOp",EDGE,"E74.1.1");Q2=makeQuery(id+"F12.imprint","IMPRINT",FACE,{"disambiguationData":[TD([[makeQuery(id+"F12.imprint","IMPRINT",EDGE,{"derivedFrom":subQ0}),-1.0]])]});}
            var Q3;
            {var subQ0=sQuery(id+"F12.wireOp",EDGE,"E73");Q3=makeQuery(id+"F12.imprint","IMPRINT",FACE,{"disambiguationData":[TD([[makeQuery(id+"F12.imprint","IMPRINT",EDGE,{"derivedFrom":subQ0}),-1.0]])]});}
            extrude(context, id + "F13", {"entities" : qUnion([Q0, Q1, Q2, Q3]), "operationType" : NewBodyOperationType.REMOVE, "endBound" : BoundingType.UP_TO_NEXT, "oppositeDirection" : true, "depth" : 25 * mm});
        }
    });
